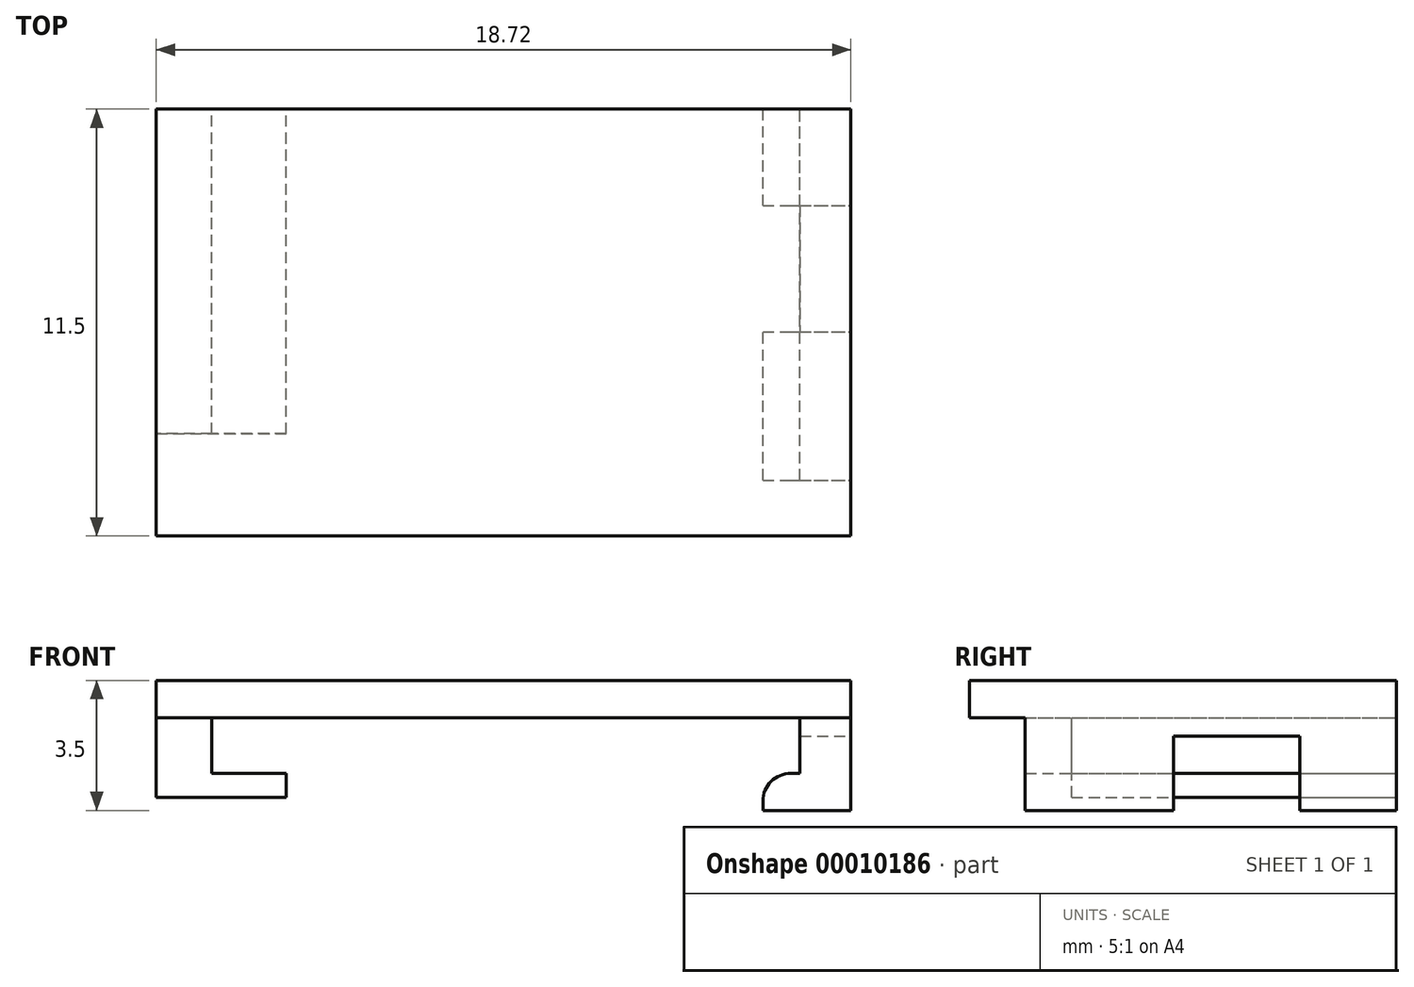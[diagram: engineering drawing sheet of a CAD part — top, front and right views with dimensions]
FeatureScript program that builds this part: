
annotation { "Feature Type Name" : "Feature", "Feature Type Description" : "" }
export const myFeature = defineFeature(function(context is Context, id is Id, definition is map)
    precondition{}
    {
        {
            var Q0;
            Q0=qCreatedBy(makeId("Front.planeOp"),FACE);
            var sketch = newSketch(context, id + "F0", { "sketchPlane" : qUnion([Q0])});
            skLineSegment(sketch, "E0", {"start": v(0, 0) * mm, "end": v(15.85, 0) * mm});
            skLineSegment(sketch, "E1", {"start": v(15.85, -2.5) * mm, "end": v(17.22, -2.5) * mm});
            skLineSegment(sketch, "E2", {"start": v(17.22, -2.5) * mm, "end": v(17.22, 1) * mm});
            skLineSegment(sketch, "E3", {"start": v(17.22, 1) * mm, "end": v(-1.5, 1) * mm});
            skLineSegment(sketch, "E4", {"start": v(-1.5, 1) * mm, "end": v(-1.5, -2.15) * mm});
            skLineSegment(sketch, "E5", {"start": v(0, -1.5) * mm, "end": v(0, 0) * mm});
            skLineSegment(sketch, "E6", {"start": v(-1.5, -2.15) * mm, "end": v(2, -2.15) * mm});
            skLineSegment(sketch, "E7", {"start": v(2, -2.15) * mm, "end": v(2, -1.5) * mm});
            skLineSegment(sketch, "E8", {"start": v(2, -1.5) * mm, "end": v(0, -1.5) * mm});
            skLineSegment(sketch, "E9.bottom", {"start": v(15.85, -2.5) * mm, "end": v(14.85, -2.5) * mm});
            skLineSegment(sketch, "E9.top", {"start": v(15.85, -1.5) * mm, "end": v(15.6, -1.5) * mm});
            skLineSegment(sketch, "E9.right", {"start": v(14.85, -2.5) * mm, "end": v(14.85, -2.25) * mm});
            skLineSegment(sketch, "E10", {"start": v(15.85, -1.5) * mm, "end": v(15.85, 0) * mm});
            skPoint(sketch, "E11.visualSharp", {"position": v(14.85, -1.5) * mm});
            skArc(sketch, "E11.filletArc", {"start": v(15.6, -1.5) * mm, "mid": v(15.07, -1.72) * mm, "end": v(14.85, -2.25) * mm});
            skSolve(sketch);
        }
        {
            var Q0;
            Q0 = qSketchRegion(id + "F0", true);
            extrude(context, id + "F1", {"entities" : qUnion([Q0]), "depth" : 11.5 * mm});
        }
        {
            var Q0;
            Q0=makeQuery(id+"F1.opExtrude","SWEPT_FACE",FACE,{"disambiguationData":[OSD([sQuery(id+"F0.wireOp",EDGE,"E2")])]});
            var sketch = newSketch(context, id + "F2", { "sketchPlane" : qUnion([Q0])});
            skLineSegment(sketch, "E12.bottom", {"start": v(-6, -4.07) * mm, "end": v(-2.6, -4.07) * mm});
            skLineSegment(sketch, "E12.top", {"start": v(-6, -0.5) * mm, "end": v(-2.6, -0.5) * mm});
            skLineSegment(sketch, "E12.left", {"start": v(-6, -4.07) * mm, "end": v(-6, -0.5) * mm});
            skLineSegment(sketch, "E12.right", {"start": v(-2.6, -4.07) * mm, "end": v(-2.6, -0.5) * mm});
            skSolve(sketch);
        }
        {
            var Q0;
            Q0 = qSketchRegion(id + "F2", true);
            extrude(context, id + "F3", {"entities" : qUnion([Q0]), "operationType" : NewBodyOperationType.REMOVE, "oppositeDirection" : true, "depth" : 5 * mm});
        }
        {
            var Q0;
            Q0=makeQuery(id+"F1.opExtrude","SWEPT_FACE",FACE,{"disambiguationData":[OSD([sQuery(id+"F0.wireOp",EDGE,"E4")])]});
            var sketch = newSketch(context, id + "F4", { "sketchPlane" : qUnion([Q0])});
            skLineSegment(sketch, "E13.bottom", {"start": v(12.5, 0) * mm, "end": v(8.75, 0) * mm});
            skLineSegment(sketch, "E13.top", {"start": v(12.5, -4.3) * mm, "end": v(8.75, -4.3) * mm});
            skLineSegment(sketch, "E13.left", {"start": v(8.75, -4.3) * mm, "end": v(8.75, 0) * mm});
            skLineSegment(sketch, "E13.right", {"start": v(12.5, -4.3) * mm, "end": v(12.5, 0) * mm});
            skSolve(sketch);
        }
        {
            var Q0;
            Q0 = qSketchRegion(id + "F4", true);
            extrude(context, id + "F5", {"entities" : qUnion([Q0]), "operationType" : NewBodyOperationType.REMOVE, "oppositeDirection" : true, "depth" : 5 * mm});
        }
        {
            var Q0;
            Q0=makeQuery(id+"F1.opExtrude","SWEPT_FACE",FACE,{"disambiguationData":[OSD([sQuery(id+"F0.wireOp",EDGE,"E2")])]});
            var sketch = newSketch(context, id + "F6", { "sketchPlane" : qUnion([Q0])});
            skLineSegment(sketch, "E14.bottom", {"start": v(-11.5, -2.5) * mm, "end": v(-10, -2.5) * mm});
            skLineSegment(sketch, "E14.top", {"start": v(-11.5, 0) * mm, "end": v(-10, 0) * mm});
            skLineSegment(sketch, "E14.left", {"start": v(-11.5, -2.5) * mm, "end": v(-11.5, 0) * mm});
            skLineSegment(sketch, "E14.right", {"start": v(-10, -2.5) * mm, "end": v(-10, 0) * mm});
            skSolve(sketch);
        }
        {
            var Q0;
            Q0 = qSketchRegion(id + "F6", true);
            var Q1;
            Q1=makeQuery(id+"F1.opExtrude","SWEPT_FACE",FACE,{"disambiguationData":[OSD([sQuery(id+"F0.wireOp",EDGE,"E7")])]});
            extrude(context, id + "F7", {"entities" : qUnion([Q0]), "operationType" : NewBodyOperationType.REMOVE, "endBound" : BoundingType.UP_TO_SURFACE, "oppositeDirection" : true, "endBoundEntityFace" : qUnion([Q1]), "depth" : 25 * mm});
        }
    });
